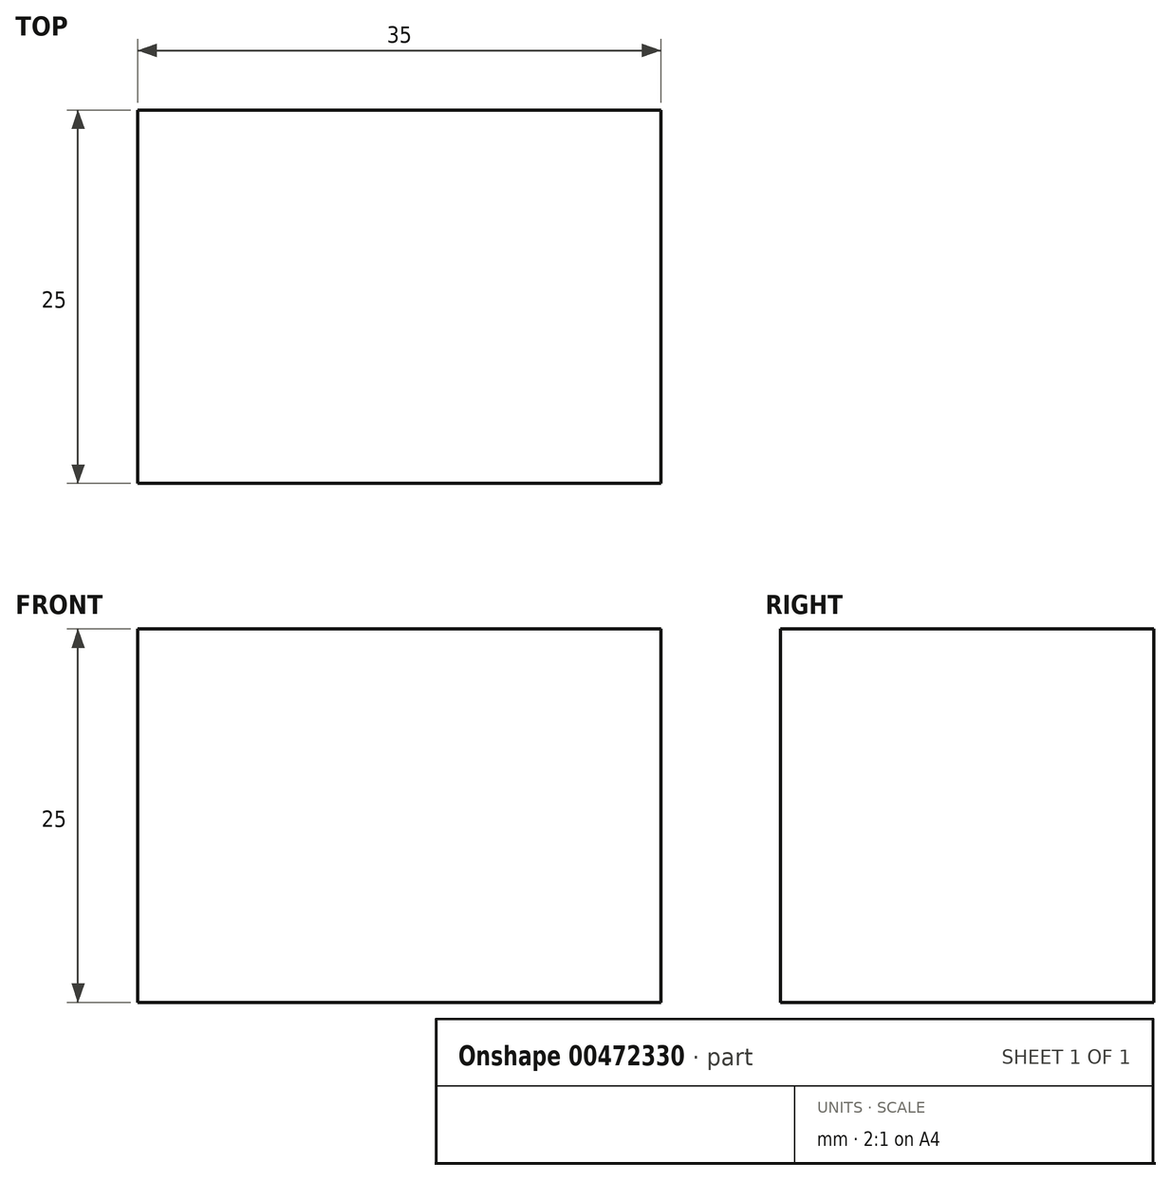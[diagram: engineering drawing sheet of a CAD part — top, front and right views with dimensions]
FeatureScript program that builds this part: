
annotation { "Feature Type Name" : "Feature", "Feature Type Description" : "" }
export const myFeature = defineFeature(function(context is Context, id is Id, definition is map)
    precondition{}
    {
        {
            var Q0;
            Q0=qCreatedBy(makeId("Front.planeOp"),FACE);
            var sketch = newSketch(context, id + "F0", { "sketchPlane" : qUnion([Q0])});
            skLineSegment(sketch, "E0", {"start": v(-19.71, 19.8) * mm, "end": v(5.29, 19.8) * mm});
            skLineSegment(sketch, "E1", {"start": v(5.29, 19.8) * mm, "end": v(5.29, -5.2) * mm});
            skLineSegment(sketch, "E2", {"start": v(5.29, -5.2) * mm, "end": v(-19.71, -5.2) * mm});
            skLineSegment(sketch, "E3", {"start": v(-19.71, -5.2) * mm, "end": v(-19.71, 19.8) * mm});
            skLineSegment(sketch, "E4", {"start": v(5.29, 19.8) * mm, "end": v(10.29, 19.8) * mm});
            skLineSegment(sketch, "E5", {"start": v(10.29, 19.8) * mm, "end": v(10.29, -5.2) * mm});
            skLineSegment(sketch, "E6", {"start": v(10.29, -5.2) * mm, "end": v(5.29, -5.2) * mm});
            skLineSegment(sketch, "E7", {"start": v(-19.71, 19.8) * mm, "end": v(-24.71, 19.8) * mm});
            skLineSegment(sketch, "E8", {"start": v(-24.71, 19.8) * mm, "end": v(-24.71, -5.2) * mm});
            skLineSegment(sketch, "E9", {"start": v(-24.71, -5.2) * mm, "end": v(-19.71, -5.2) * mm});
            skSolve(sketch);
        }
        {
            var Q0;
            Q0 = qSketchRegion(id + "F0", true);
            extrude(context, id + "F1", {"entities" : qUnion([Q0]), "depth" : 25 * mm});
        }
    });
